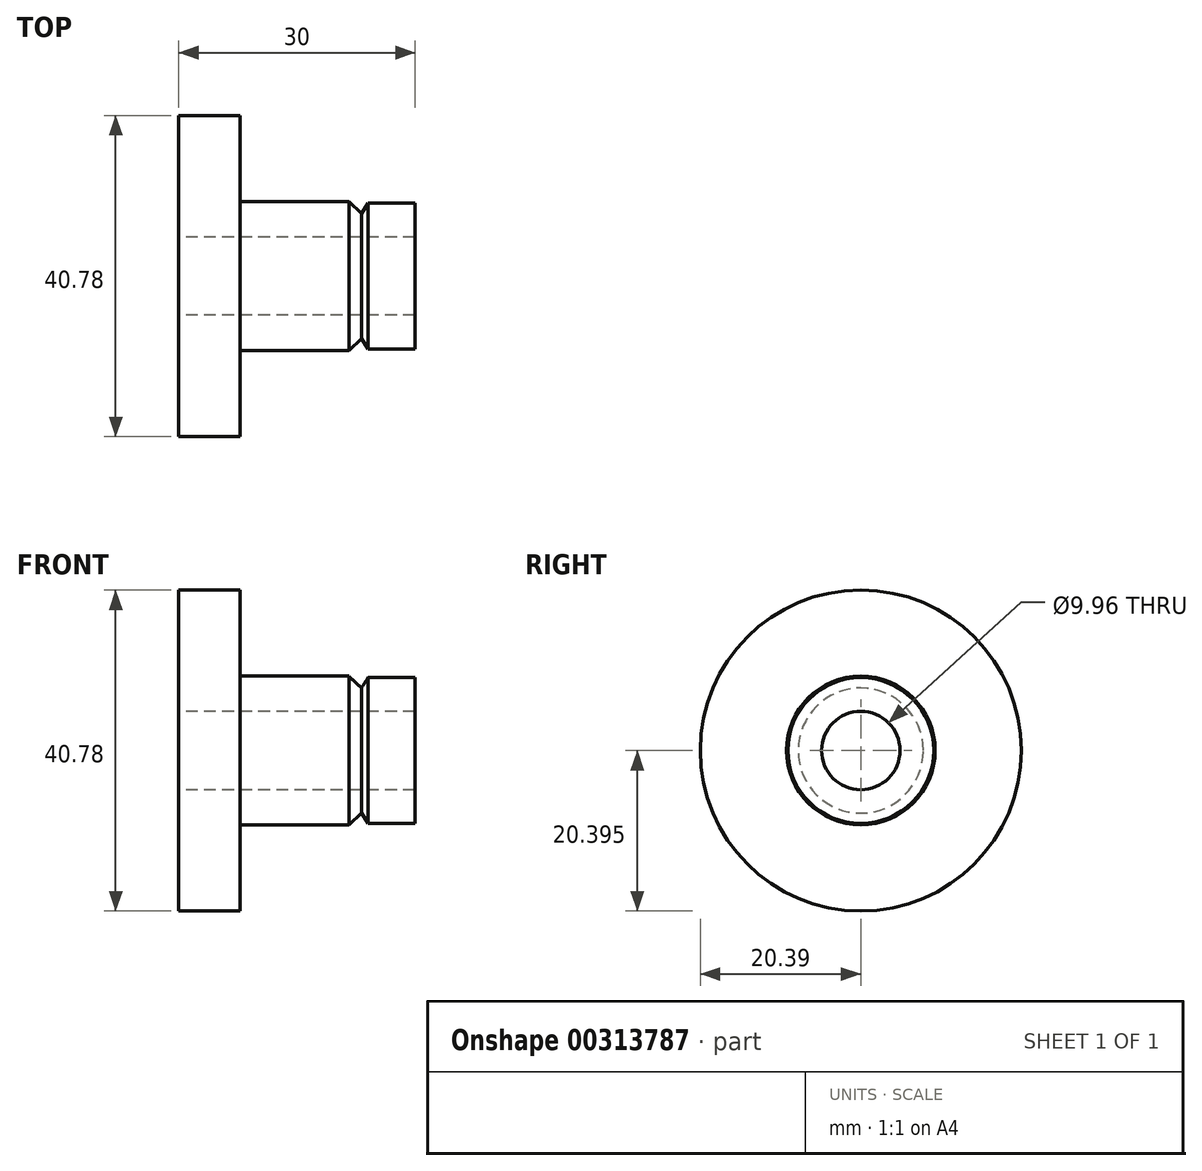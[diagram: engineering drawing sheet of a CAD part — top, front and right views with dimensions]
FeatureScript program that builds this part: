
annotation { "Feature Type Name" : "Feature", "Feature Type Description" : "" }
export const myFeature = defineFeature(function(context is Context, id is Id, definition is map)
    precondition{}
    {
        {
            var Q0;
            Q0=qCreatedBy(makeId("Front.planeOp"),FACE);
            var sketch = newSketch(context, id + "F0", { "sketchPlane" : qUnion([Q0])});
            skLineSegment(sketch, "E0", {"start": v(-17.64, 8.26) * mm, "end": v(12.36, 8.26) * mm});
            skLineSegment(sketch, "E1", {"start": v(12.36, 8.26) * mm, "end": v(12.36, 12.55) * mm});
            skLineSegment(sketch, "E2", {"start": v(12.36, 12.55) * mm, "end": v(6.4, 12.55) * mm});
            skLineSegment(sketch, "E3", {"start": v(6.4, 12.55) * mm, "end": v(5.57, 11.23) * mm});
            skLineSegment(sketch, "E4", {"start": v(5.57, 11.23) * mm, "end": v(3.98, 12.73) * mm});
            skLineSegment(sketch, "E5", {"start": v(3.98, 12.73) * mm, "end": v(-9.84, 12.73) * mm});
            skLineSegment(sketch, "E6", {"start": v(-9.84, 12.73) * mm, "end": v(-9.84, 23.67) * mm});
            skLineSegment(sketch, "E7", {"start": v(-9.84, 23.67) * mm, "end": v(-17.64, 23.67) * mm});
            skLineSegment(sketch, "E8", {"start": v(-17.64, 23.67) * mm, "end": v(-17.64, 8.26) * mm});
            skSolve(sketch);
        }
        {
            var Q0;
            Q0=qCreatedBy(makeId("Front.planeOp"),FACE);
            var sketch = newSketch(context, id + "F1", { "sketchPlane" : qUnion([Q0])});
            skPoint(sketch, "E9", {"position": v(-16.67, 3.28) * mm});
            skSolve(sketch);
        }
        {
            var Q0;
            Q0=qCreatedBy(makeId("Front.planeOp"),FACE);
            var sketch = newSketch(context, id + "F2", { "sketchPlane" : qUnion([Q0])});
            skLineSegment(sketch, "E10", {"start": v(-16.67, 3.28) * mm, "end": v(6.07, 3.28) * mm});
            skSolve(sketch);
        }
        {
            var Q0;
            Q0=makeQuery(id+"F0.imprint","IMPRINT",FACE,{"disambiguationData":[TD([[makeQuery(id+"F0.imprint","IMPRINT",EDGE,{"derivedFrom":sQuery(id+"F0.wireOp",EDGE,"E0")}),1.0]])]});
            var Q1;
            Q1=sQuery(id+"F2.wireOp",EDGE,"E10");
            revolve(context, id + "F3", {"entities" : qUnion([Q0]), "axis" : qUnion([Q1]), "revolveType" : RevolveType.FULL});
        }
    });
